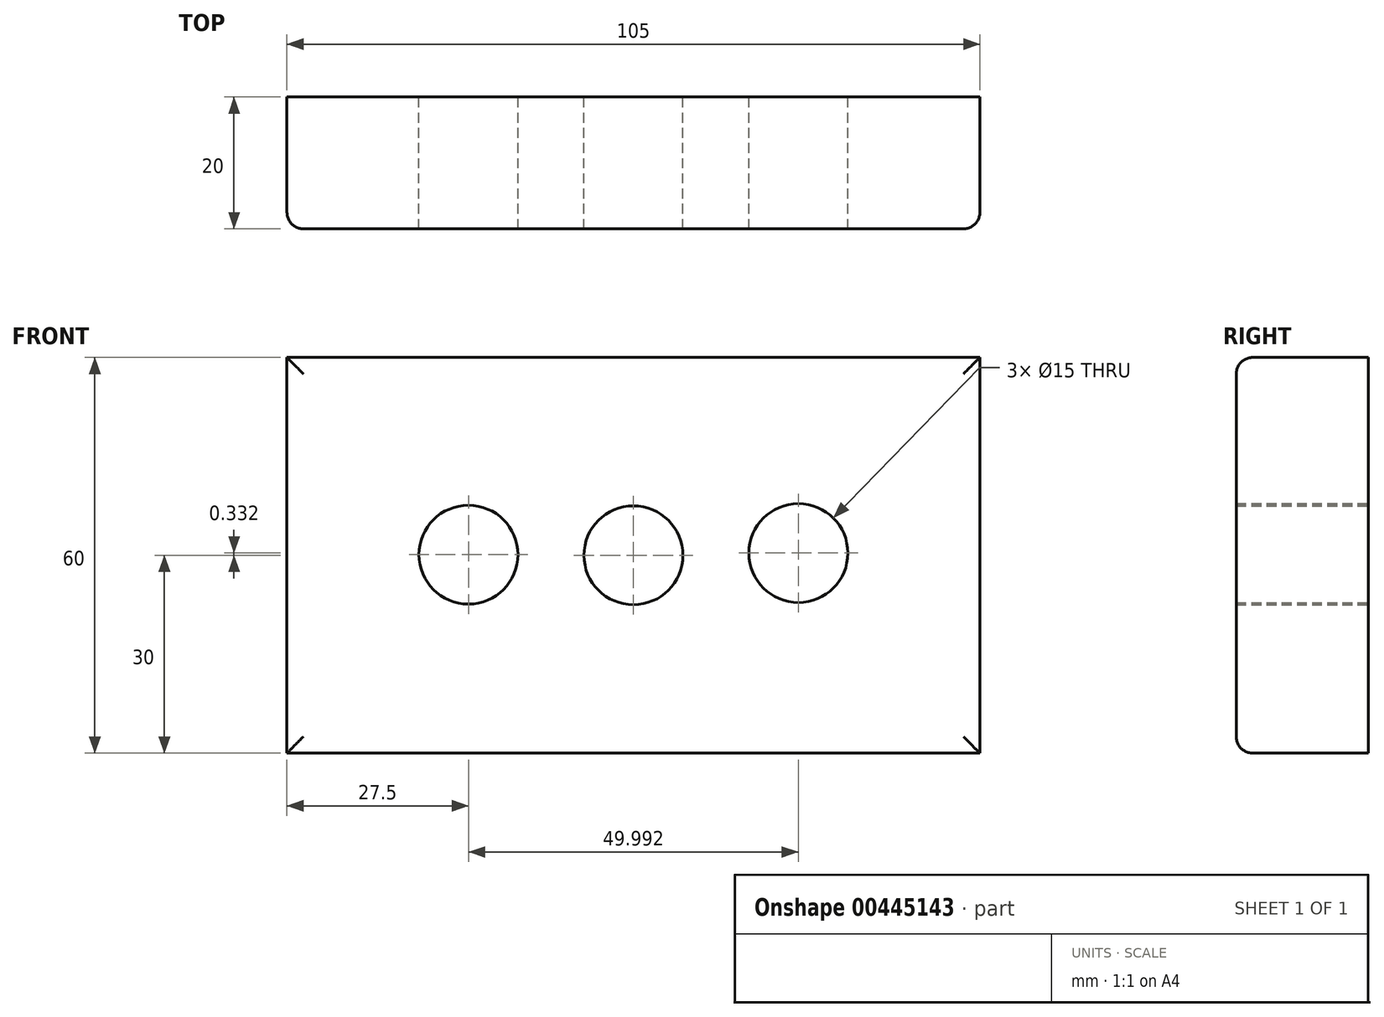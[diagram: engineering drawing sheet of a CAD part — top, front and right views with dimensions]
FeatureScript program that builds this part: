
annotation { "Feature Type Name" : "Feature", "Feature Type Description" : "" }
export const myFeature = defineFeature(function(context is Context, id is Id, definition is map)
    precondition{}
    {
        {
            var Q0;
            Q0=qCreatedBy(makeId("Front.planeOp"),FACE);
            var sketch = newSketch(context, id + "F0", { "sketchPlane" : qUnion([Q0])});
            skLineSegment(sketch, "E0.bottom", {"start": v(52.5, 30) * mm, "end": v(-52.5, 30) * mm});
            skLineSegment(sketch, "E0.top", {"start": v(52.5, -30) * mm, "end": v(-52.5, -30) * mm});
            skLineSegment(sketch, "E0.left", {"start": v(52.5, 30) * mm, "end": v(52.5, -30) * mm});
            skLineSegment(sketch, "E0.right", {"start": v(-52.5, 30) * mm, "end": v(-52.5, -30) * mm});
            skPoint(sketch, "E0.middle", {"position": v(0, 0) * mm});
            skCircle(sketch, "E1", {"center": v(0, 0) * mm, "radius": 7.5 * mm});
            skLineSegment(sketch, "E2", {"start": v(7.5, 0) * mm, "end": v(17.5, 0) * mm});
            skLineSegment(sketch, "E3", {"start": v(-7.5, 0) * mm, "end": v(-17.5, 0) * mm});
            skCircle(sketch, "E4", {"center": v(25, 0.33) * mm, "radius": 7.5 * mm});
            skPoint(sketch, "E4.second.point", {"position": v(32.49, 0) * mm});
            skPoint(sketch, "E4.third.point", {"position": v(25.66, -7.14) * mm});
            skCircle(sketch, "E5", {"center": v(-25, 0.09) * mm, "radius": 7.5 * mm});
            skPoint(sketch, "E5.second.point", {"position": v(-32.5, 0) * mm});
            skPoint(sketch, "E5.third.point", {"position": v(-29.66, -5.79) * mm});
            skSolve(sketch);
        }
        {
            var Q0;
            Q0=makeQuery(id+"F0.imprint","IMPRINT",FACE,{"disambiguationData":[TD([[makeQuery(id+"F0.imprint","IMPRINT",EDGE,{"derivedFrom":sQuery(id+"F0.wireOp",EDGE,"E0.bottom")}),1.0]])]});
            extrude(context, id + "F1", {"entities" : qUnion([Q0]), "endBound" : BoundingType.SYMMETRIC, "depth" : 20 * mm});
        }
        {
            var Q0;
            Q0=makeQuery(id+"F1.opExtrude","CAP_EDGE",EDGE,{"disambiguationData":[OSD([sQuery(id+"F0.wireOp",EDGE,"E0.bottom")])],"isStart":false});
            var Q1;
            Q1=makeQuery(id+"F1.opExtrude","CAP_EDGE",EDGE,{"disambiguationData":[OSD([sQuery(id+"F0.wireOp",EDGE,"E0.right")])],"isStart":false});
            var Q2;
            Q2=makeQuery(id+"F1.opExtrude","CAP_EDGE",EDGE,{"disambiguationData":[OSD([sQuery(id+"F0.wireOp",EDGE,"E0.top")])],"isStart":false});
            var Q3;
            Q3=makeQuery(id+"F1.opExtrude","CAP_EDGE",EDGE,{"disambiguationData":[OSD([sQuery(id+"F0.wireOp",EDGE,"E0.left")])],"isStart":false});
            fillet(context, id + "F2", {"entities" : qUnion([Q0, Q1, Q2, Q3]), "radius" : 2.5 * mm, "tangentPropagation" : true, "allowEdgeOverflow" : false});
        }
    });
